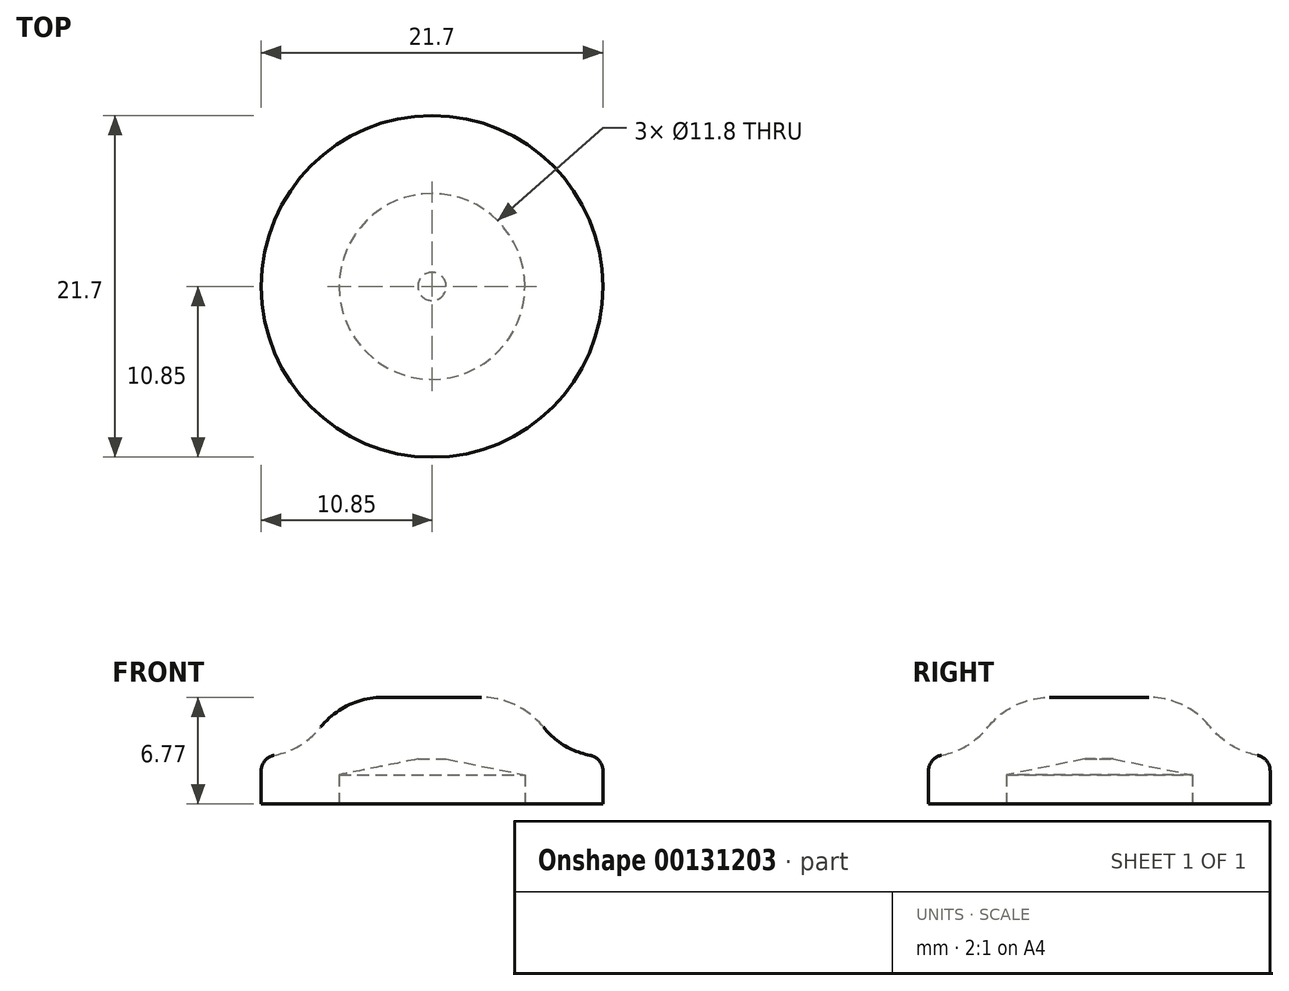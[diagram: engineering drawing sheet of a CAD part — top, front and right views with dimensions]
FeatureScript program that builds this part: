
annotation { "Feature Type Name" : "Feature", "Feature Type Description" : "" }
export const myFeature = defineFeature(function(context is Context, id is Id, definition is map)
    precondition{}
    {
        {
            var Q0;
            Q0=qCreatedBy(makeId("Front.planeOp"),FACE);
            var sketch = newSketch(context, id + "F0", { "sketchPlane" : qUnion([Q0])});
            skLineSegment(sketch, "E0", {"start": v(0, 13.69) * mm, "end": v(8, 13.69) * mm});
            skLineSegment(sketch, "E1", {"start": v(8, 13.69) * mm, "end": v(8, 9.92) * mm});
            skLineSegment(sketch, "E2", {"start": v(8, 9.92) * mm, "end": v(10.85, 9.92) * mm});
            skLineSegment(sketch, "E3", {"start": v(10.85, 9.92) * mm, "end": v(10.85, 6.92) * mm});
            skLineSegment(sketch, "E4", {"start": v(10.85, 6.92) * mm, "end": v(0, 6.92) * mm});
            skLineSegment(sketch, "E5", {"start": v(0, 6.92) * mm, "end": v(0, 13.69) * mm});
            skSolve(sketch);
        }
        {
            var Q0;
            Q0=makeQuery(id+"F0.imprint","IMPRINT",FACE,{"disambiguationData":[TD([[makeQuery(id+"F0.imprint","IMPRINT",EDGE,{"derivedFrom":sQuery(id+"F0.wireOp",EDGE,"E0")}),-1.0]])]});
            var Q1;
            Q1=sQuery(id+"F0.wireOp",EDGE,"E5");
            revolve(context, id + "F1", {"entities" : qUnion([Q0]), "axis" : qUnion([Q1]), "revolveType" : RevolveType.FULL});
        }
        {
            var Q0;
            Q0=makeQuery(id+"F1.opRevolve","SWEPT_EDGE",EDGE,{"disambiguationData":[OSD([sQuery(id+"F0.wireOp",EDGE,"E0"),sQuery(id+"F0.wireOp",EDGE,"E1")])]});
            fillet(context, id + "F2", {"entities" : qUnion([Q0]), "radius" : 5 * mm, "tangentPropagation" : true, "allowEdgeOverflow" : false});
        }
        {
            var Q0;
            Q0=makeQuery(id+"F2.opFillet","BLEND_EDGE",EDGE,{"blendedFrom":[makeQuery(id+"F1.opRevolve","SWEPT_EDGE",EDGE,{"disambiguationData":[OSD([sQuery(id+"F0.wireOp",EDGE,"E0"),sQuery(id+"F0.wireOp",EDGE,"E1")])]}),makeQuery(id+"F1.opRevolve","SWEPT_FACE",FACE,{"disambiguationData":[OSD([sQuery(id+"F0.wireOp",EDGE,"E2")])]})],"blendedInto":[makeQuery(id+"F1.opRevolve","SWEPT_FACE",FACE,{"disambiguationData":[OSD([sQuery(id+"F0.wireOp",EDGE,"E2")])]})]});
            fillet(context, id + "F3", {"entities" : qUnion([Q0]), "radius" : 5 * mm, "tangentPropagation" : true, "allowEdgeOverflow" : false});
        }
        {
            var Q0;
            Q0=makeQuery(id+"F3.opFillet","BLEND_EDGE",EDGE,{"blendedFrom":[makeQuery(id+"F2.opFillet","BLEND_EDGE",EDGE,{"blendedFrom":[makeQuery(id+"F1.opRevolve","SWEPT_EDGE",EDGE,{"disambiguationData":[OSD([sQuery(id+"F0.wireOp",EDGE,"E0"),sQuery(id+"F0.wireOp",EDGE,"E1")])]}),makeQuery(id+"F1.opRevolve","SWEPT_FACE",FACE,{"disambiguationData":[OSD([sQuery(id+"F0.wireOp",EDGE,"E2")])]})],"blendedInto":[makeQuery(id+"F1.opRevolve","SWEPT_FACE",FACE,{"disambiguationData":[OSD([sQuery(id+"F0.wireOp",EDGE,"E2")])]})]}),makeQuery(id+"F1.opRevolve","SWEPT_FACE",FACE,{"disambiguationData":[OSD([sQuery(id+"F0.wireOp",EDGE,"E3")])]})],"blendedInto":[makeQuery(id+"F1.opRevolve","SWEPT_FACE",FACE,{"disambiguationData":[OSD([sQuery(id+"F0.wireOp",EDGE,"E3")])]})]});
            fillet(context, id + "F4", {"entities" : qUnion([Q0]), "radius" : 1 * mm, "tangentPropagation" : true, "allowEdgeOverflow" : false});
        }
        {
            var Q0;
            Q0=makeQuery(id+"F1.opRevolve","SWEPT_FACE",FACE,{"disambiguationData":[OSD([sQuery(id+"F0.wireOp",EDGE,"E4")])]});
            var sketch = newSketch(context, id + "F5", { "sketchPlane" : qUnion([Q0])});
            skCircle(sketch, "E6", {"center": v(0, 0) * mm, "radius": 5.9 * mm});
            skSolve(sketch);
        }
        {
            var Q0;
            Q0=makeQuery(id+"F5.imprint","IMPRINT",FACE,{"disambiguationData":[TD([[makeQuery(id+"F5.imprint","IMPRINT",EDGE,{"derivedFrom":sQuery(id+"F5.wireOp",EDGE,"E6")}),1.0]])]});
            extrude(context, id + "F6", {"entities" : qUnion([Q0]), "operationType" : NewBodyOperationType.REMOVE, "oppositeDirection" : true, "depth" : 2.85 * mm});
        }
        {
            var Q0;
            Q0=makeQuery(id+"F6.boolean.opBoolean","COPY",EDGE,{"derivedFrom":makeQuery(id+"F6.opExtrude","CAP_EDGE",EDGE,{"disambiguationData":[OSD([sQuery(id+"F5.wireOp",EDGE,"E6")])],"isStart":false})});
            chamfer(context, id + "F7", {"entities" : qUnion([Q0]), "chamferType" : ChamferType.TWO_OFFSETS, "width1" : 5 * mm, "oppositeDirection" : false, "width2" : 1 * mm, "tangentPropagation" : true});
        }
    });
